FCSTD DOCUMENT  (FreeCAD 0.20R29603 (Git))
Label: tc2-plugs-pcb
License: All rights reserved
LicenseURL: http://en.wikipedia.org/wiki/All_rights_reserved
objects: Sketcher::SketchObject×2
note: 2 computed .brp shape members not serialized (recipe doc carries the construction recipe); baked Part::Feature solids carry a one-line shape summary decoded from their .brp

FEATURE [Sketcher::SketchObject] Sketch  label="boarder"
  FullyConstrained = true
  sketch-geometry (16):
    g0: LineSegment StartX=35 StartY=23.3 StartZ=0 EndX=35 EndY=-3 EndZ=0
    g1: LineSegment StartX=34 StartY=-4 StartZ=0 EndX=-29 EndY=-4 EndZ=0
    g2: LineSegment StartX=-30 StartY=-3 StartZ=0 EndX=-30 EndY=19.5 EndZ=0
    g3: LineSegment StartX=-29 StartY=20.5 StartZ=0 EndX=-9.5 EndY=20.5 EndZ=0
    g4: LineSegment StartX=-8.5 StartY=19.5 StartZ=0 EndX=-8.5 EndY=5.5 EndZ=0
    g5: LineSegment StartX=-7 StartY=4 StartZ=0 EndX=7 EndY=4 EndZ=0
    g6: LineSegment StartX=8.5 StartY=5.5 StartZ=0 EndX=8.5 EndY=23.3 EndZ=0
    g7: LineSegment StartX=9.5 StartY=24.3 StartZ=0 EndX=34 EndY=24.3 EndZ=0
    g8: ArcOfCircle CenterX=-9.5 CenterY=19.5 CenterZ=0 NormalX=0 NormalY=0 NormalZ=1 AngleXU=0 Radius=1 StartAngle=0 EndAngle=1.5708
    g9: ArcOfCircle CenterX=-7 CenterY=5.5 CenterZ=0 NormalX=0 NormalY=0 NormalZ=1 AngleXU=0 Radius=1.5 StartAngle=3.14159 EndAngle=4.71239
    g10: ArcOfCircle CenterX=7 CenterY=5.5 CenterZ=0 NormalX=0 NormalY=0 NormalZ=1 AngleXU=0 Radius=1.5 StartAngle=4.71239 EndAngle=6.28319
    g11: ArcOfCircle CenterX=9.5 CenterY=23.3 CenterZ=0 NormalX=0 NormalY=0 NormalZ=1 AngleXU=0 Radius=1 StartAngle=1.5708 EndAngle=3.14159
    g12: ArcOfCircle CenterX=34 CenterY=23.3 CenterZ=0 NormalX=0 NormalY=0 NormalZ=1 AngleXU=0 Radius=1 StartAngle=6e-16 EndAngle=1.5708
    g13: ArcOfCircle CenterX=34 CenterY=-3 CenterZ=0 NormalX=0 NormalY=0 NormalZ=1 AngleXU=0 Radius=1 StartAngle=4.71239 EndAngle=6.28319
    g14: ArcOfCircle CenterX=-29 CenterY=-3 CenterZ=0 NormalX=0 NormalY=0 NormalZ=1 AngleXU=0 Radius=1 StartAngle=3.14159 EndAngle=4.71239
    g15: ArcOfCircle CenterX=-29 CenterY=19.5 CenterZ=0 NormalX=0 NormalY=0 NormalZ=1 AngleXU=0 Radius=1 StartAngle=1.5708 EndAngle=3.14159
  constraints (39):
    c: Horizontal(g1)
    c: Vertical(g0)
    c: Vertical(g2)
    c: Vertical(g4)
    c: Horizontal(g5)
    c: Vertical(g6)
    c: Horizontal(g7)
    c: Tangent(g3,g8) = 1.5708
    c: Tangent(g4,g8) = 1.5708
    c: Tangent(g4,g9) = -1.5708
    c: Tangent(g5,g9) = -1.5708
    c: Tangent(g5,g10) = -1.5708
    c: Tangent(g6,g10) = -1.5708
    c: Tangent(g6,g11) = 1.5708
    c: Tangent(g7,g11) = 1.5708
    c: Tangent(g0,g12) = 1.5708
    c: Tangent(g7,g12) = 1.5708
    c: Tangent(g0,g13) = 1.5708
    c: Tangent(g1,g13) = 1.5708
    c: Tangent(g1,g14) = 1.5708
    c: Tangent(g2,g14) = 1.5708
    c: Tangent(g2,g15) = 1.5708
    c: Tangent(g3,g15) = 1.5708
    c: Radius(g9) = 1.5
    c: Horizontal(g3)
    c: Equal(g15,g14)
    c: Equal(g15,g13)
    c: Equal(g15,g11)
    c: Equal(g15,g8)
    c: Radius(g15) = 1
    c: Symmetric(g4,g6,g-2)
    c: Equal(g11,g12)
    c: DistanceY(g1,g7) = 28.3
    c: DistanceY(g-1,g5) = 4
    c: DistanceY(g1,g-1) = 4
    c: DistanceY(g1,g3) = 24.5
    c: DistanceX(g2,g-1) = 30
    c: DistanceX(g-1,g0) = 35
    c: DistanceX(g5,g5) = 14
FEATURE [Sketcher::SketchObject] Sketch001  label="features"
  FullyConstrained = true
  MapMode = 5
  sketch-geometry (3):
    g0: Circle CenterX=-15 CenterY=7 CenterZ=0 NormalX=0 NormalY=0 NormalZ=1 AngleXU=0 Radius=0.5
    g1: Circle CenterX=22 CenterY=7 CenterZ=0 NormalX=0 NormalY=0 NormalZ=1 AngleXU=0 Radius=0.5
    g2: Circle CenterX=0 CenterY=0 CenterZ=0 NormalX=0 NormalY=0 NormalZ=1 AngleXU=0 Radius=0.5
  constraints (8):
    c: DistanceX(g0,g-1) = 15
    c: Horizontal(g0,g1)
    c: Equal(g1,g0)
    c: Diameter(g1) = 1
    c: Equal(g2,g0)
    c: DistanceY(g2,g0) = 7
    c: DistanceX(g0,g1) = 37
    c: Coincident(g2,g-1)
